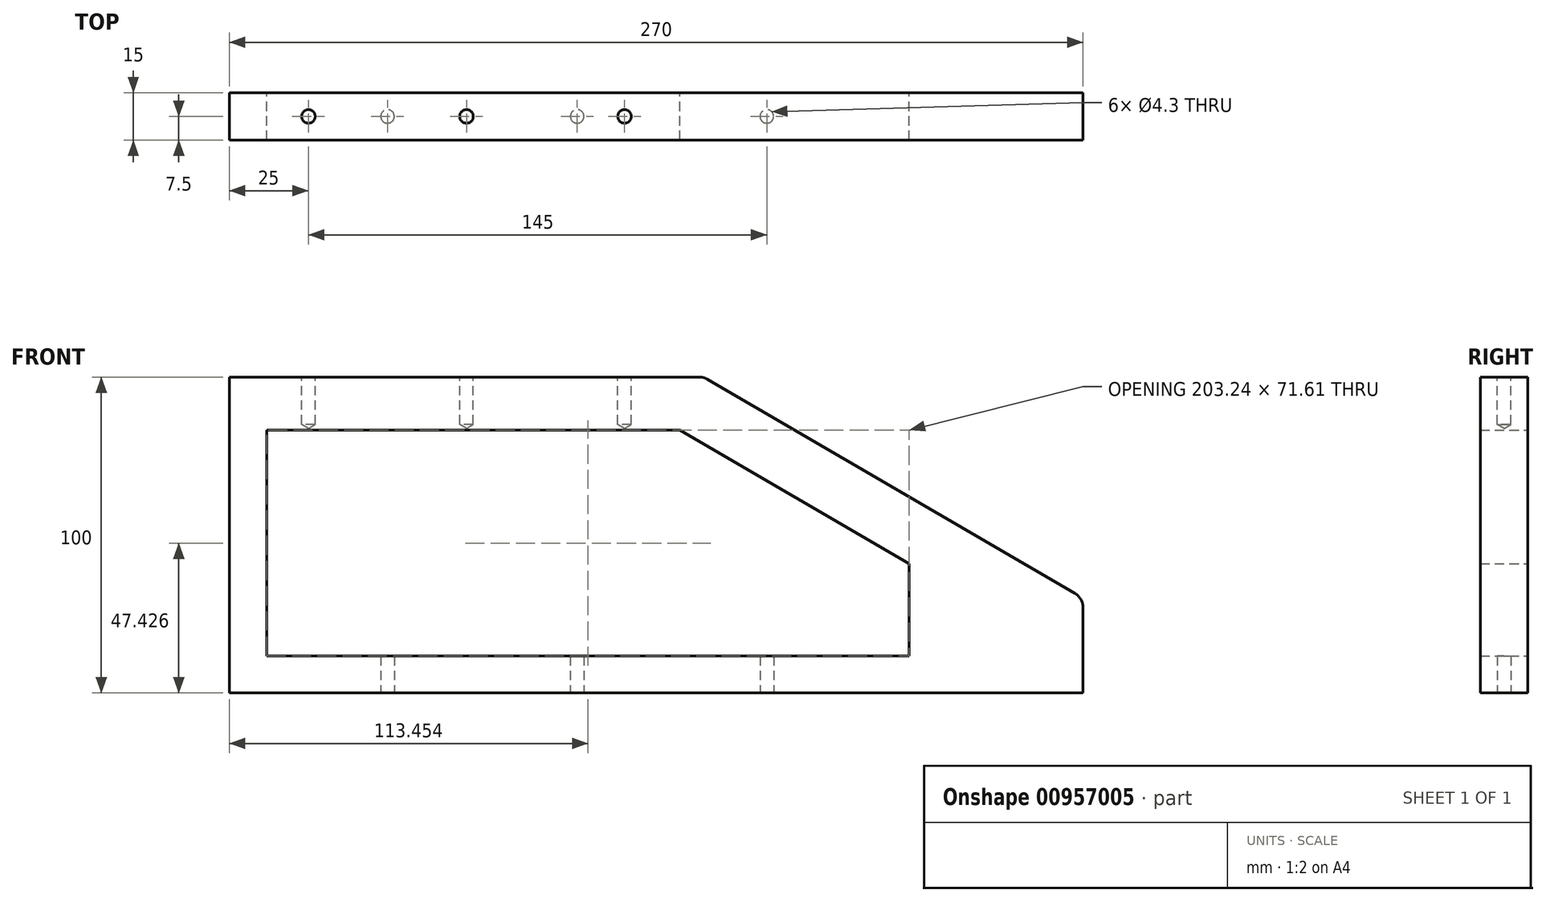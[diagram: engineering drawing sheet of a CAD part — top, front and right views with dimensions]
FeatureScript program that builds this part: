
annotation { "Feature Type Name" : "Feature", "Feature Type Description" : "" }
export const myFeature = defineFeature(function(context is Context, id is Id, definition is map)
    precondition{}
    {
        {
            var Q0;
            Q0=qCreatedBy(makeId("Front.planeOp"),FACE);
            var sketch = newSketch(context, id + "F0", { "sketchPlane" : qUnion([Q0])});
            skLineSegment(sketch, "E0.bottom", {"start": v(0, 0) * mm, "end": v(150, 0) * mm});
            skLineSegment(sketch, "E0.top", {"start": v(0, 100) * mm, "end": v(150, 100) * mm});
            skLineSegment(sketch, "E0.left", {"start": v(0, 0) * mm, "end": v(0, 100) * mm});
            skLineSegment(sketch, "E1", {"start": v(150, 100) * mm, "end": v(270, 30) * mm});
            skLineSegment(sketch, "E2", {"start": v(270, 30) * mm, "end": v(270, 0) * mm});
            skLineSegment(sketch, "E3", {"start": v(270, 0) * mm, "end": v(150, 0) * mm});
            skSolve(sketch);
        }
        {
            var Q0;
            Q0 = qSketchRegion(id + "F0", true);
            extrude(context, id + "F1", {"entities" : qUnion([Q0]), "depth" : 15 * mm, "offsetDistance" : 25 * mm});
        }
        {
            var Q0;
            Q0=makeQuery(id+"F1.opExtrude","SWEPT_FACE",FACE,{"disambiguationData":[OSD([sQuery(id+"F0.wireOp",EDGE,"E0.top")])]});
            var sketch = newSketch(context, id + "F2", { "sketchPlane" : qUnion([Q0])});
            skPoint(sketch, "E4", {"position": v(25, -7.5) * mm});
            skPoint(sketch, "E4.positionSnap0", {"position": v(0, -7.5) * mm});
            skPoint(sketch, "E5", {"position": v(75, -7.5) * mm});
            skPoint(sketch, "E6", {"position": v(125, -7.5) * mm});
            skSolve(sketch);
        }
        {
            var Q0;
            Q0=sQuery(id+"F2.wireOp",VERTEX,"E6");
            var Q1;
            Q1=sQuery(id+"F2.wireOp",VERTEX,"E5");
            var Q2;
            Q2=sQuery(id+"F2.wireOp",VERTEX,"E4");
            var Q3;
            Q3=makeQuery(id+"F1.opExtrude","SWEPT_BODY",BODY,{"disambiguationData":[OSD([sQuery(id+"F0.wireOp",EDGE,"E0.bottom"),sQuery(id+"F0.wireOp",EDGE,"E0.top"),sQuery(id+"F0.wireOp",EDGE,"E0.left"),sQuery(id+"F0.wireOp",EDGE,"E0.right")])]});
            hole(context, id + "F3", {"style" : HoleStyle.SIMPLE, "endStyle" : HoleEndStyle.BLIND, "standardTappedOrClearance" : lookupTablePath({ "standard" : "ISO", "size" : "4.3", "type" : "Drilled" }), "standardBlindInLast" : lookupTablePath({ "standard" : "ISO", "size" : "4.3", "type" : "Drilled" }), "holeDiameter" : 4.3 * mm, "majorDiameter" : 5 * mm, "holeDepth" : 15 * mm, "isTappedThrough" : true, "tappedDepth" : 12 * mm, "tapClearance" : 3, "locations" : qUnion([Q0, Q1, Q2]), "scope" : qUnion([Q3])});
        }
        {
            var Q0;
            Q0=makeQuery(id+"F1.opExtrude","SWEPT_EDGE",EDGE,{"disambiguationData":[OSD([sQuery(id+"F0.wireOp",EDGE,"E1"),sQuery(id+"F0.wireOp",EDGE,"E2")])]});
            fillet(context, id + "F4", {"entities" : qUnion([Q0]), "radius" : 5 * mm, "tangentPropagation" : true, "allowEdgeOverflow" : false});
        }
        {
            var Q0;
            Q0=makeQuery(id+"F1.opExtrude","SWEPT_EDGE",EDGE,{"disambiguationData":[OSD([sQuery(id+"F0.wireOp",EDGE,"E0.top"),sQuery(id+"F0.wireOp",EDGE,"E1")])]});
            fillet(context, id + "F5", {"entities" : qUnion([Q0]), "radius" : 5 * mm, "tangentPropagation" : true, "allowEdgeOverflow" : false});
        }
        {
            var Q0;
            Q0=qCreatedBy(makeId("Front.planeOp"),FACE);
            var sketch = newSketch(context, id + "F6", { "sketchPlane" : qUnion([Q0])});
            skLineSegment(sketch, "E7", {"start": v(11.83, 11.62) * mm, "end": v(215.08, 11.62) * mm});
            skLineSegment(sketch, "E8", {"start": v(215.08, 11.62) * mm, "end": v(215.08, 40.92) * mm});
            skLineSegment(sketch, "E9", {"start": v(11.83, 11.62) * mm, "end": v(11.83, 83.23) * mm});
            skLineSegment(sketch, "E10", {"start": v(11.83, 83.23) * mm, "end": v(142.55, 83.23) * mm});
            skLineSegment(sketch, "E11", {"start": v(142.55, 83.23) * mm, "end": v(215.08, 40.92) * mm});
            skSolve(sketch);
        }
        {
            var Q0;
            Q0 = qSketchRegion(id + "F6", true);
            extrude(context, id + "F7", {"entities" : qUnion([Q0]), "operationType" : NewBodyOperationType.REMOVE, "endBound" : BoundingType.THROUGH_ALL, "depth" : 25 * mm, "offsetDistance" : 25 * mm});
        }
        {
            var Q0;
            Q0=makeQuery(id+"F1.opExtrude","SWEPT_FACE",FACE,{"disambiguationData":[OSD([sQuery(id+"F0.wireOp",EDGE,"E0.bottom"),sQuery(id+"F0.wireOp",EDGE,"E3")])]});
            var sketch = newSketch(context, id + "F8", { "sketchPlane" : qUnion([Q0])});
            skPoint(sketch, "E12", {"position": v(0, 7.5) * mm});
            skPoint(sketch, "E13", {"position": v(50, 7.5) * mm});
            skPoint(sketch, "E14", {"position": v(110, 7.5) * mm});
            skPoint(sketch, "E15", {"position": v(170, 7.5) * mm});
            skSolve(sketch);
        }
        {
            var Q0;
            Q0=sQuery(id+"F8.wireOp",VERTEX,"E13");
            var Q1;
            Q1=sQuery(id+"F8.wireOp",VERTEX,"E14");
            var Q2;
            Q2=sQuery(id+"F8.wireOp",VERTEX,"E15");
            var Q3;
            Q3=makeQuery(id+"F1.opExtrude","SWEPT_BODY",BODY,{"disambiguationData":[OSD([sQuery(id+"F0.wireOp",EDGE,"E0.bottom"),sQuery(id+"F0.wireOp",EDGE,"E0.top"),sQuery(id+"F0.wireOp",EDGE,"E0.left"),sQuery(id+"F0.wireOp",EDGE,"E1"),sQuery(id+"F0.wireOp",EDGE,"E2"),sQuery(id+"F0.wireOp",EDGE,"E3")])]});
            hole(context, id + "F9", {"style" : HoleStyle.SIMPLE, "endStyle" : HoleEndStyle.BLIND, "standardTappedOrClearance" : lookupTablePath({ "standard" : "ISO", "size" : "4.3", "type" : "Drilled" }), "standardBlindInLast" : lookupTablePath({ "standard" : "ISO", "size" : "4.3", "type" : "Drilled" }), "holeDiameter" : 4.3 * mm, "majorDiameter" : 5 * mm, "holeDepth" : 20 * mm, "isTappedThrough" : true, "tappedDepth" : 12 * mm, "tapClearance" : 3, "locations" : qUnion([Q0, Q1, Q2]), "scope" : qUnion([Q3])});
        }
    });
